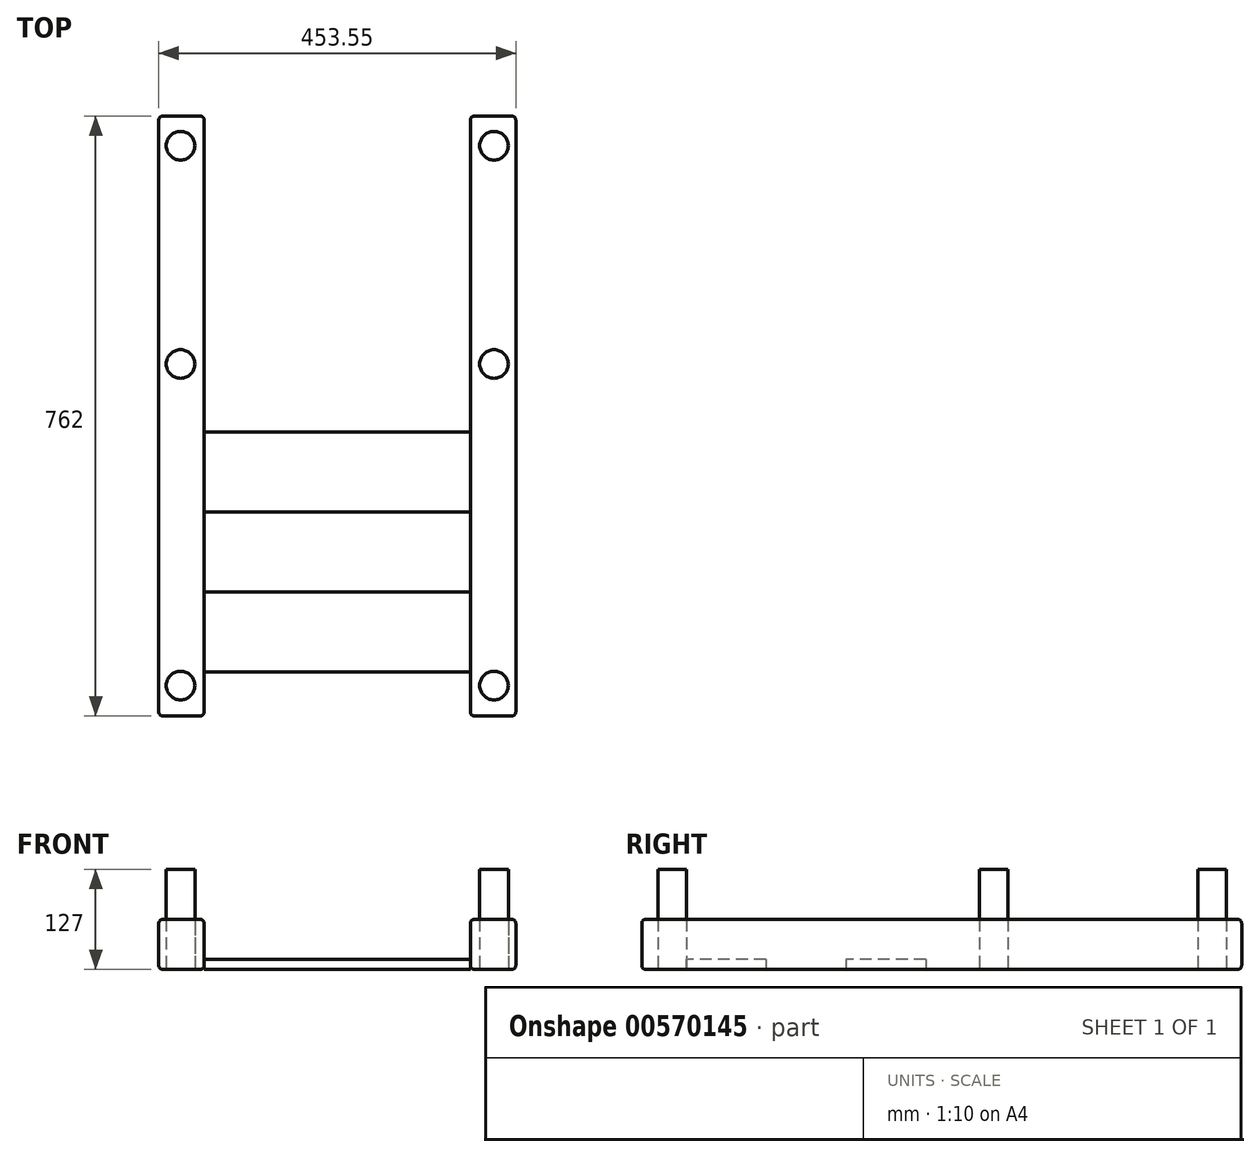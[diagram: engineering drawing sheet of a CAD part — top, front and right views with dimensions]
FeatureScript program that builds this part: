
annotation { "Feature Type Name" : "Feature", "Feature Type Description" : "" }
export const myFeature = defineFeature(function(context is Context, id is Id, definition is map)
    precondition{}
    {
        {
            var Q0;
            Q0=qCreatedBy(makeId("Top.planeOp"),FACE);
            var sketch = newSketch(context, id + "F0", { "sketchPlane" : qUnion([Q0])});
            skLineSegment(sketch, "E0.bottom", {"start": v(-168.86, 475.8) * mm, "end": v(-226.57, 475.8) * mm});
            skLineSegment(sketch, "E0.top", {"start": v(-168.86, -286.2) * mm, "end": v(-226.57, -286.2) * mm});
            skLineSegment(sketch, "E0.left", {"start": v(-168.86, 475.8) * mm, "end": v(-168.86, -286.2) * mm});
            skLineSegment(sketch, "E0.right", {"start": v(-226.57, 475.8) * mm, "end": v(-226.57, -286.2) * mm});
            skLineSegment(sketch, "E1.bottom", {"start": v(169.27, 475.8) * mm, "end": v(226.98, 475.8) * mm});
            skLineSegment(sketch, "E1.top", {"start": v(169.27, -286.2) * mm, "end": v(226.98, -286.2) * mm});
            skLineSegment(sketch, "E1.left", {"start": v(169.27, 475.8) * mm, "end": v(169.27, -286.2) * mm});
            skLineSegment(sketch, "E1.right", {"start": v(226.98, 475.8) * mm, "end": v(226.98, -286.2) * mm});
            skLineSegment(sketch, "E2.bottom", {"start": v(-168.86, -230.12) * mm, "end": v(169.27, -230.12) * mm});
            skLineSegment(sketch, "E2.top", {"start": v(-168.86, -128.52) * mm, "end": v(169.27, -128.52) * mm});
            skLineSegment(sketch, "E2.left", {"start": v(-168.86, -230.12) * mm, "end": v(-168.86, -128.52) * mm});
            skLineSegment(sketch, "E2.right", {"start": v(169.27, -230.12) * mm, "end": v(169.27, -128.52) * mm});
            skLineSegment(sketch, "E3.bottom", {"start": v(-168.86, -26.92) * mm, "end": v(169.27, -26.92) * mm});
            skLineSegment(sketch, "E3.top", {"start": v(-168.86, 74.68) * mm, "end": v(169.27, 74.68) * mm});
            skLineSegment(sketch, "E3.left", {"start": v(-168.86, -26.92) * mm, "end": v(-168.86, 74.68) * mm});
            skLineSegment(sketch, "E3.right", {"start": v(169.27, -26.92) * mm, "end": v(169.27, 74.68) * mm});
            skSolve(sketch);
        }
        {
            var Q0;
            {var subQ3=sQuery(id+"F0.wireOp",EDGE,"E0.bottom");Q0=makeQuery(id+"F0.imprint","IMPRINT",FACE,{"disambiguationData":[TD([[makeQuery(id+"F0.imprint","IMPRINT",EDGE,{"derivedFrom":subQ3}),1.0]])]});}
            var Q1;
            {var subQ3=sQuery(id+"F0.wireOp",EDGE,"E1.bottom");Q1=makeQuery(id+"F0.imprint","IMPRINT",FACE,{"disambiguationData":[TD([[makeQuery(id+"F0.imprint","IMPRINT",EDGE,{"derivedFrom":subQ3}),-1.0]])]});}
            extrude(context, id + "F1", {"entities" : qUnion([Q0, Q1]), "depth" : 63.5 * mm, "offsetDistance" : 25.4 * mm});
        }
        {
            var Q0;
            Q0=makeQuery(id+"F0.imprint","IMPRINT",FACE,{"disambiguationData":[TD([[makeQuery(id+"F0.imprint","IMPRINT",EDGE,{"derivedFrom":sQuery(id+"F0.wireOp",EDGE,"E2.bottom")}),1.0]])]});
            var Q1;
            Q1=makeQuery(id+"F0.imprint","IMPRINT",FACE,{"disambiguationData":[TD([[makeQuery(id+"F0.imprint","IMPRINT",EDGE,{"derivedFrom":sQuery(id+"F0.wireOp",EDGE,"E3.bottom")}),1.0]])]});
            extrude(context, id + "F2", {"entities" : qUnion([Q0, Q1]), "depth" : 12.7 * mm, "offsetDistance" : 25.4 * mm});
        }
        {
            var Q0;
            {var subQ0=sQuery(id+"F0.wireOp",EDGE,"E2.top");Q0=makeQuery(id+"F0.imprint","IMPRINT",FACE,{"disambiguationData":[TD([[makeQuery(id+"F0.imprint","IMPRINT",EDGE,{"derivedFrom":subQ0}),1.0]])]});}
            var sketch = newSketch(context, id + "F3", { "sketchPlane" : qUnion([Q0])});
            skCircle(sketch, "E4", {"center": v(-198.88, -247.64) * mm, "radius": 18.2 * mm});
            skCircle(sketch, "E5", {"center": v(199.3, -247.64) * mm, "radius": 18.2 * mm});
            skCircle(sketch, "E6", {"center": v(199.3, 160.84) * mm, "radius": 18.2 * mm});
            skCircle(sketch, "E7", {"center": v(199.3, 438.16) * mm, "radius": 18.2 * mm});
            skCircle(sketch, "E8", {"center": v(-198.88, 438.16) * mm, "radius": 18.2 * mm});
            skCircle(sketch, "E9", {"center": v(-198.88, 160.84) * mm, "radius": 18.2 * mm});
            skSolve(sketch);
        }
        {
            var Q0;
            Q0=makeQuery(id+"F3.imprint","IMPRINT",FACE,{"disambiguationData":[TD([[makeQuery(id+"F3.imprint","IMPRINT",EDGE,{"derivedFrom":sQuery(id+"F3.wireOp",EDGE,"E8")}),1.0]])]});
            var Q1;
            Q1=makeQuery(id+"F3.imprint","IMPRINT",FACE,{"disambiguationData":[TD([[makeQuery(id+"F3.imprint","IMPRINT",EDGE,{"derivedFrom":sQuery(id+"F3.wireOp",EDGE,"E7")}),1.0]])]});
            var Q2;
            Q2=makeQuery(id+"F3.imprint","IMPRINT",FACE,{"disambiguationData":[TD([[makeQuery(id+"F3.imprint","IMPRINT",EDGE,{"derivedFrom":sQuery(id+"F3.wireOp",EDGE,"E6")}),1.0]])]});
            var Q3;
            Q3=makeQuery(id+"F3.imprint","IMPRINT",FACE,{"disambiguationData":[TD([[makeQuery(id+"F3.imprint","IMPRINT",EDGE,{"derivedFrom":sQuery(id+"F3.wireOp",EDGE,"E5")}),1.0]])]});
            var Q4;
            Q4=makeQuery(id+"F3.imprint","IMPRINT",FACE,{"disambiguationData":[TD([[makeQuery(id+"F3.imprint","IMPRINT",EDGE,{"derivedFrom":sQuery(id+"F3.wireOp",EDGE,"E4")}),1.0]])]});
            var Q5;
            Q5=makeQuery(id+"F3.imprint","IMPRINT",FACE,{"disambiguationData":[TD([[makeQuery(id+"F3.imprint","IMPRINT",EDGE,{"derivedFrom":sQuery(id+"F3.wireOp",EDGE,"E9")}),1.0]])]});
            extrude(context, id + "F4", {"entities" : qUnion([Q0, Q1, Q2, Q3, Q4, Q5]), "depth" : 127 * mm, "offsetDistance" : 25.4 * mm});
        }
        {
            var Q0;
            Q0=makeQuery(id+"F1.opExtrude","CAP_EDGE",EDGE,{"disambiguationData":[OSD([sQuery(id+"F0.wireOp",EDGE,"E1.right")])],"isStart":true});
            var Q1;
            Q1=makeQuery(id+"F1.opExtrude","CAP_EDGE",EDGE,{"disambiguationData":[OSD([sQuery(id+"F0.wireOp",EDGE,"E1.right")])],"isStart":false});
            var Q2;
            Q2=makeQuery(id+"F1.opExtrude","CAP_EDGE",EDGE,{"disambiguationData":[OSD([sQuery(id+"F0.wireOp",EDGE,"E1.top")])],"isStart":false});
            var Q3;
            Q3=makeQuery(id+"F1.opExtrude","CAP_EDGE",EDGE,{"disambiguationData":[OSD([sQuery(id+"F0.wireOp",EDGE,"E1.top")])],"isStart":true});
            var Q4;
            Q4=makeQuery(id+"F1.opExtrude","SWEPT_EDGE",EDGE,{"disambiguationData":[OSD([sQuery(id+"F0.wireOp",EDGE,"E1.top"),sQuery(id+"F0.wireOp",EDGE,"E1.left")])]});
            var Q5;
            Q5=makeQuery(id+"F1.opExtrude","CAP_EDGE",EDGE,{"disambiguationData":[OSD([sQuery(id+"F0.wireOp",EDGE,"E1.left"),sQuery(id+"F0.wireOp",EDGE,"E2.right"),sQuery(id+"F0.wireOp",EDGE,"E3.right")])],"isStart":false});
            var Q6;
            Q6=makeQuery(id+"F1.opExtrude","CAP_EDGE",EDGE,{"disambiguationData":[OSD([sQuery(id+"F0.wireOp",EDGE,"E1.left"),sQuery(id+"F0.wireOp",EDGE,"E2.right"),sQuery(id+"F0.wireOp",EDGE,"E3.right")])],"isStart":true});
            var Q7;
            Q7=makeQuery(id+"F1.opExtrude","CAP_EDGE",EDGE,{"disambiguationData":[OSD([sQuery(id+"F0.wireOp",EDGE,"E1.bottom")])],"isStart":true});
            var Q8;
            Q8=makeQuery(id+"F1.opExtrude","SWEPT_EDGE",EDGE,{"disambiguationData":[OSD([sQuery(id+"F0.wireOp",EDGE,"E1.bottom"),sQuery(id+"F0.wireOp",EDGE,"E1.right")])]});
            var Q9;
            Q9=makeQuery(id+"F1.opExtrude","SWEPT_EDGE",EDGE,{"disambiguationData":[OSD([sQuery(id+"F0.wireOp",EDGE,"E1.bottom"),sQuery(id+"F0.wireOp",EDGE,"E1.left")])]});
            var Q10;
            Q10=makeQuery(id+"F1.opExtrude","CAP_EDGE",EDGE,{"disambiguationData":[OSD([sQuery(id+"F0.wireOp",EDGE,"E1.bottom")])],"isStart":false});
            var Q11;
            Q11=makeQuery(id+"F1.opExtrude","SWEPT_EDGE",EDGE,{"disambiguationData":[OSD([sQuery(id+"F0.wireOp",EDGE,"E1.top"),sQuery(id+"F0.wireOp",EDGE,"E1.right")])]});
            var Q12;
            Q12=makeQuery(id+"F1.opExtrude","SWEPT_EDGE",EDGE,{"disambiguationData":[OSD([sQuery(id+"F0.wireOp",EDGE,"E0.top"),sQuery(id+"F0.wireOp",EDGE,"E0.left")])]});
            var Q13;
            Q13=makeQuery(id+"F1.opExtrude","SWEPT_EDGE",EDGE,{"disambiguationData":[OSD([sQuery(id+"F0.wireOp",EDGE,"E0.top"),sQuery(id+"F0.wireOp",EDGE,"E0.right")])]});
            var Q14;
            Q14=makeQuery(id+"F1.opExtrude","CAP_EDGE",EDGE,{"disambiguationData":[OSD([sQuery(id+"F0.wireOp",EDGE,"E0.top")])],"isStart":true});
            var Q15;
            Q15=makeQuery(id+"F1.opExtrude","CAP_EDGE",EDGE,{"disambiguationData":[OSD([sQuery(id+"F0.wireOp",EDGE,"E0.top")])],"isStart":false});
            var Q16;
            Q16=makeQuery(id+"F1.opExtrude","CAP_EDGE",EDGE,{"disambiguationData":[OSD([sQuery(id+"F0.wireOp",EDGE,"E0.right")])],"isStart":false});
            var Q17;
            Q17=makeQuery(id+"F1.opExtrude","CAP_EDGE",EDGE,{"disambiguationData":[OSD([sQuery(id+"F0.wireOp",EDGE,"E0.right")])],"isStart":true});
            var Q18;
            Q18=makeQuery(id+"F1.opExtrude","SWEPT_EDGE",EDGE,{"disambiguationData":[OSD([sQuery(id+"F0.wireOp",EDGE,"E0.bottom"),sQuery(id+"F0.wireOp",EDGE,"E0.right")])]});
            var Q19;
            Q19=makeQuery(id+"F1.opExtrude","SWEPT_EDGE",EDGE,{"disambiguationData":[OSD([sQuery(id+"F0.wireOp",EDGE,"E0.bottom"),sQuery(id+"F0.wireOp",EDGE,"E0.left")])]});
            var Q20;
            Q20=makeQuery(id+"F1.opExtrude","CAP_EDGE",EDGE,{"disambiguationData":[OSD([sQuery(id+"F0.wireOp",EDGE,"E0.bottom")])],"isStart":true});
            var Q21;
            Q21=makeQuery(id+"F1.opExtrude","CAP_EDGE",EDGE,{"disambiguationData":[OSD([sQuery(id+"F0.wireOp",EDGE,"E0.bottom")])],"isStart":false});
            var Q22;
            Q22=makeQuery(id+"F1.opExtrude","CAP_EDGE",EDGE,{"disambiguationData":[OSD([sQuery(id+"F0.wireOp",EDGE,"E0.left"),sQuery(id+"F0.wireOp",EDGE,"E2.left"),sQuery(id+"F0.wireOp",EDGE,"E3.left")])],"isStart":false});
            var Q23;
            Q23=makeQuery(id+"F1.opExtrude","CAP_EDGE",EDGE,{"disambiguationData":[OSD([sQuery(id+"F0.wireOp",EDGE,"E0.left"),sQuery(id+"F0.wireOp",EDGE,"E2.left"),sQuery(id+"F0.wireOp",EDGE,"E3.left")])],"isStart":true});
            fillet(context, id + "F5", {"entities" : qUnion([Q0, Q1, Q2, Q3, Q4, Q5, Q6, Q7, Q8, Q9, Q10, Q11, Q12, Q13, Q14, Q15, Q16, Q17, Q18, Q19, Q20, Q21, Q22, Q23]), "radius" : 5.08 * mm, "tangentPropagation" : true, "allowEdgeOverflow" : false});
        }
    });
